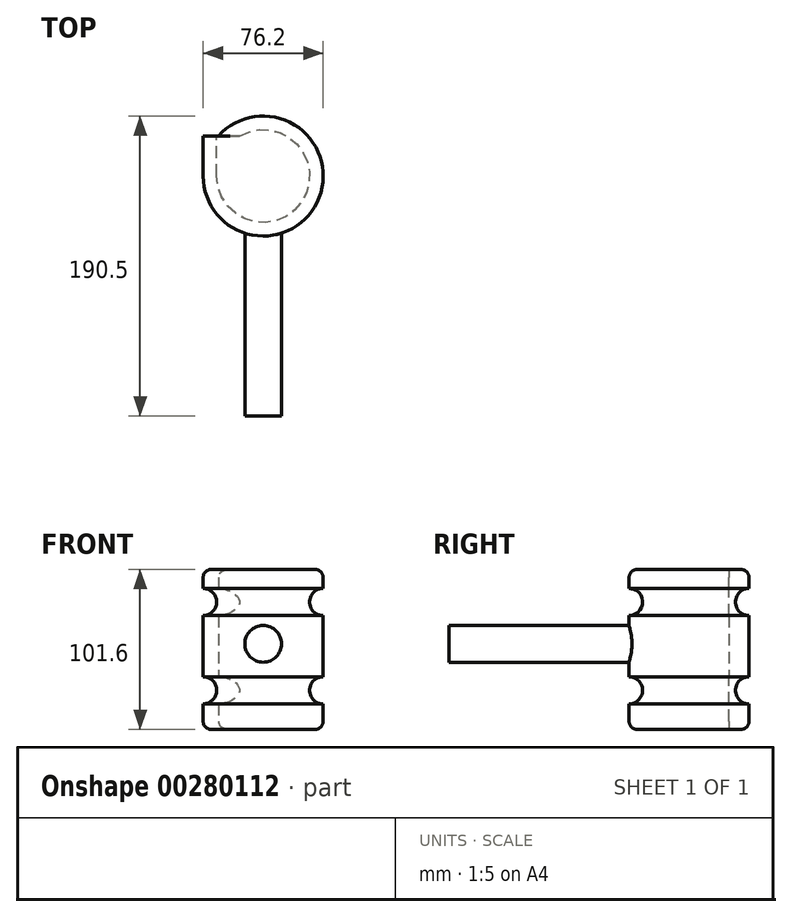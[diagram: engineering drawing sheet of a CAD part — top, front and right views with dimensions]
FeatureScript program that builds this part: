
annotation { "Feature Type Name" : "Feature", "Feature Type Description" : "" }
export const myFeature = defineFeature(function(context is Context, id is Id, definition is map)
    precondition{}
    {
        {
            var Q0;
            Q0=qCreatedBy(makeId("Front.planeOp"),FACE);
            var sketch = newSketch(context, id + "F0", { "sketchPlane" : qUnion([Q0])});
            skLineSegment(sketch, "E0.bottom", {"start": v(0, 0) * mm, "end": v(-38.1, 0) * mm});
            skLineSegment(sketch, "E0.top", {"start": v(0, 101.6) * mm, "end": v(-38.1, 101.6) * mm});
            skLineSegment(sketch, "E0.left", {"start": v(0, 0) * mm, "end": v(0, 101.6) * mm});
            skLineSegment(sketch, "E0.right", {"start": v(-38.1, 0) * mm, "end": v(-38.1, 16.27) * mm});
            skArc(sketch, "E1", {"start": v(-38.1, 16.27) * mm, "mid": v(-29.48, 24.88) * mm, "end": v(-38.1, 33.5) * mm});
            skArc(sketch, "E2", {"start": v(-38.1, 72.3) * mm, "mid": v(-29.5, 80.9) * mm, "end": v(-38.1, 89.5) * mm});
            skLineSegment(sketch, "E3.trimOffspring", {"start": v(-38.1, 33.5) * mm, "end": v(-38.1, 72.3) * mm});
            skLineSegment(sketch, "E4.trimOffspring", {"start": v(-38.1, 89.5) * mm, "end": v(-38.1, 101.6) * mm});
            skSolve(sketch);
        }
        {
            var Q0;
            Q0 = qSketchRegion(id + "F0", true);
            extrude(context, id + "F1", {"entities" : qUnion([Q0]), "depth" : 25.4 * mm});
        }
        {
            var Q0;
            Q0=makeQuery(id+"F1.opExtrude","CAP_FACE",FACE,{"disambiguationData":[OSD([sQuery(id+"F0.wireOp",EDGE,"E0.bottom"),sQuery(id+"F0.wireOp",EDGE,"E0.top"),sQuery(id+"F0.wireOp",EDGE,"E0.left"),sQuery(id+"F0.wireOp",EDGE,"E0.right"),sQuery(id+"F0.wireOp",EDGE,"E1"),sQuery(id+"F0.wireOp",EDGE,"E2"),sQuery(id+"F0.wireOp",EDGE,"E3.trimOffspring"),sQuery(id+"F0.wireOp",EDGE,"E4.trimOffspring")])],"isStart":false});
            var Q1;
            Q1=makeQuery(id+"F1.opExtrude","CAP_EDGE",EDGE,{"disambiguationData":[OSD([sQuery(id+"F0.wireOp",EDGE,"E0.left")])],"isStart":false});
            revolve(context, id + "F2", {"operationType" : NewBodyOperationType.ADD, "entities" : qUnion([Q0]), "axis" : qUnion([Q1]), "revolveType" : RevolveType.FULL});
        }
        {
            var Q0;
            Q0=qCreatedBy(makeId("Front.planeOp"),FACE);
            var sketch = newSketch(context, id + "F3", { "sketchPlane" : qUnion([Q0])});
            skCircle(sketch, "E5", {"center": v(0, 54.36) * mm, "radius": 11.64 * mm});
            skSolve(sketch);
        }
        {
            var Q0;
            Q0 = qSketchRegion(id + "F3", true);
            extrude(context, id + "F4", {"entities" : qUnion([Q0]), "operationType" : NewBodyOperationType.ADD, "depth" : 177.8 * mm});
        }
        {
            var Q0;
            Q0=makeQuery(id+"F2.opRevolve","SWEPT_EDGE",EDGE,{"disambiguationData":[OSD([sQuery(id+"F0.wireOp",EDGE,"E0.top"),sQuery(id+"F0.wireOp",EDGE,"E4.trimOffspring")])]});
            var Q1;
            Q1=makeQuery(id+"F2.opRevolve","SWEPT_EDGE",EDGE,{"disambiguationData":[OSD([sQuery(id+"F0.wireOp",EDGE,"E0.bottom"),sQuery(id+"F0.wireOp",EDGE,"E0.right")])]});
            fillet(context, id + "F5", {"entities" : qUnion([Q0, Q1]), "radius" : 5.08 * mm, "tangentPropagation" : true, "allowEdgeOverflow" : false});
        }
    });
